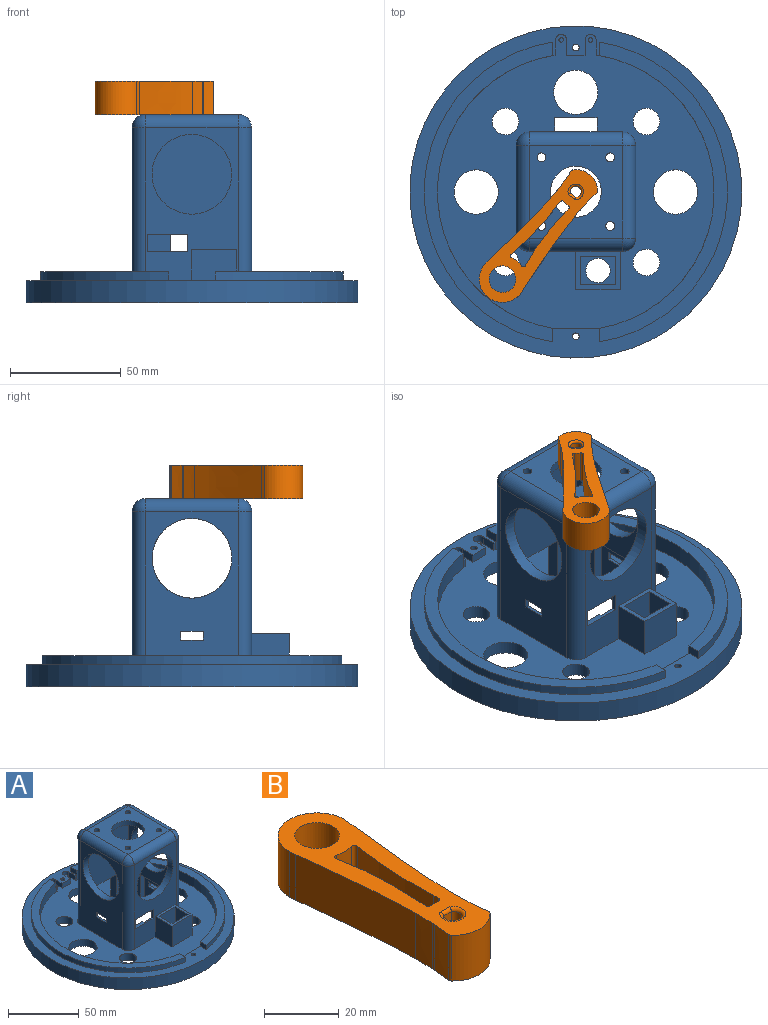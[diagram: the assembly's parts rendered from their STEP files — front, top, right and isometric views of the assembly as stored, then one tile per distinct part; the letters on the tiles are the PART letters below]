
ASSEMBLY  parts=2 mates=1
PART A: 108 faces, bbox 150x150x85 mm
  f0: plane 31.12x5.44mm, normal (0,0,-1), area 142.5mm2, adj f1,f89,f90,f103,f104,f105
  f1: plane 73x42mm, normal (0,1,0), area 2588mm2, adj f0,f11,f64,f70,f73,f89,f103
  f2: plane 10x1.44mm, normal (0,0,-1), area 14.4mm2, adj f3,f5,f17,f101
  f3: plane 4x1.44mm, normal (0,-1,0), area 5.8mm2, adj f2,f4,f17,f101
  f4: plane 10x1.44mm, normal (0,0,1), area 14.4mm2, adj f3,f5,f17,f101
  f5: plane 4x1.44mm, normal (0,1,0), area 5.8mm2, adj f2,f4,f17,f101
  f6: cylinder r=18mm len=36mm, axis (-1,0,0), area 615.2mm2, adj f17,f105
  f7: plane 8x2.64mm, normal (1,0,0), area 21.2mm2, adj f8,f12,f45,f99
  f8: plane 18x2.64mm, normal (0,0,1), area 38.5mm2, adj f7,f9,f12,f97,f98,f99
  f9: plane 8x1.44mm, normal (-1,0,0), area 11.5mm2, adj f8,f12,f45,f97
  f10: cylinder r=18mm len=36mm, axis (0,-1,0), area 615.2mm2, adj f12,f95
  f11: plane 132.88x125mm, normal (0,0,1), area 7587.8mm2, adj f1,f12,f14,f15,f17,f18,f20,f21
  f12: plane 73x42mm, normal (0,-1,0), area 1544.1mm2, adj f7,f8,f9,f10,f11,f45,f62,f66
  f13: plane 16x13mm, normal (0,0,1), area 113mm2, adj f36,f78,f79,f80,f81
  f14: plane 8.29x4mm, normal (0,-1,0), area 33.2mm2, adj f11,f16,f56,f61
  f15: plane 4x0.88mm, normal (0,-1,0), area 3.5mm2, adj f11,f16,f29,f58
  f16: plane 150x150mm, normal (0,0,1), area 3101.6mm2, adj f14,f15,f20,f21,f22,f23,f24,f26
  f17: plane 73x42mm, normal (-1,0,0), area 2008.1mm2, adj f2,f3,f4,f5,f6,f11,f67,f71
  f18: plane 73x42mm, normal (1,0,0), area 2008.1mm2, adj f11,f51,f52,f53,f54,f55,f62,f64
  f19: plane 43.12x43.12mm, normal (0,0,-1), area 1393.6mm2, adj f46,f47,f48,f49,f50,f90,f94,f95
  f20: plane 20x4mm, normal (0,1,0), area 80mm2, adj f11,f16,f29,f34
  f21: plane 4x0.88mm, normal (0,-1,0), area 3.5mm2, adj f11,f16,f34,f59
  f22: cylinder r=1.5mm len=6mm, axis (0,0,-1), area 56.5mm2, adj f16,f75
  f23: cylinder r=75mm len=150mm, axis (0,0,-1), area 4712.4mm2, adj f16,f25
  f24: cylinder r=1.5mm len=6mm, axis (0,0,-1), area 56.5mm2, adj f16,f74
  f25: plane 150x150mm, normal (0,0,-1), area 13601.3mm2, adj f23,f36,f37,f38,f39,f40,f41,f42
  f26: plane 6.08x4mm, normal (1,0,0), area 24.3mm2, adj f16,f28,f29,f30
  f27: plane 6.08x4mm, normal (1,0,0), area 24.3mm2, adj f16,f28,f29,f30
  f28: cylinder r=68.5mm len=135.38mm, axis (0,0,-1), area 776.5mm2, adj f16,f26,f27,f30
  f29: cylinder r=62.5mm len=123.39mm, axis (0,0,-1), area 1406.1mm2, adj f11,f15,f16,f20,f26,f27,f30
  f30: plane 135.38x58mm, normal (0,0,1), area 1108.1mm2, adj f26,f27,f28,f29
  f31: plane 6.08x4mm, normal (-1,0,0), area 24.3mm2, adj f16,f33,f34,f35
  f32: plane 6.08x4mm, normal (-1,0,0), area 24.3mm2, adj f16,f33,f34,f35
  f33: cylinder r=68.5mm len=135.38mm, axis (0,0,-1), area 776.5mm2, adj f16,f31,f32,f35
  f34: cylinder r=62.5mm len=123.39mm, axis (0,0,-1), area 1406.1mm2, adj f11,f16,f20,f21,f31,f32,f35
  f35: plane 135.38x58mm, normal (0,0,1), area 1108.1mm2, adj f31,f32,f33,f34
  f36: cylinder r=5.5mm len=11mm, axis (0,0,-1), area 207.3mm2, adj f13,f25
  f37: cylinder r=6mm len=12mm, axis (0,0,-1), area 226.2mm2, adj f11,f25
  f38: cylinder r=10mm len=20mm, axis (0,0,-1), area 377mm2, adj f11,f25
  f39: cylinder r=6mm len=12mm, axis (0,0,-1), area 226.2mm2, adj f11,f25
  f40: cylinder r=6mm len=12mm, axis (0,0,-1), area 226.2mm2, adj f11,f25
  f41: cylinder r=10mm len=20mm, axis (0,0,-1), area 377mm2, adj f11,f25
  f42: cylinder r=10mm len=20mm, axis (0,0,-1), area 377mm2, adj f11,f25
  f43: cylinder r=6mm len=12mm, axis (0,0,-1), area 226.2mm2, adj f11,f25
  f44: plane 42x42mm, normal (0,0,1), area 1298.3mm2, adj f46,f47,f48,f49,f50,f65,f66,f70
  f45: plane 31.12x5.44mm, normal (0,0,-1), area 148.5mm2, adj f7,f9,f12,f95,f96,f97,f99,f105
  f46: cylinder r=11.5mm len=23mm, axis (0,0,1), area 289mm2, adj f19,f44
  f47: cylinder r=2mm len=4mm, axis (0,0,1), area 50.3mm2, adj f19,f44
  f48: cylinder r=2mm len=4mm, axis (0,0,1), area 50.3mm2, adj f19,f44
  f49: cylinder r=2mm len=4mm, axis (0,0,1), area 50.3mm2, adj f19,f44
  f50: cylinder r=2mm len=4mm, axis (0,0,1), area 50.3mm2, adj f19,f44
  f51: plane 4x1.44mm, normal (0,1,0), area 5.8mm2, adj f18,f52,f54,f92
  f52: plane 10x1.44mm, normal (0,0,1), area 14.4mm2, adj f18,f51,f53,f92
  f53: plane 4x1.44mm, normal (0,-1,0), area 5.8mm2, adj f18,f52,f54,f92
  f54: plane 10x1.44mm, normal (0,0,-1), area 14.4mm2, adj f18,f51,f53,f92
  f55: cylinder r=18mm len=36mm, axis (-1,0,0), area 615.2mm2, adj f18,f94
  f56: plane 6.79x4mm, normal (-1,0,0), area 27.2mm2, adj f11,f14,f16,f57
  f57: cylinder r=2.5mm len=5mm, axis (0,0,-1), area 33.3mm2, adj f11,f16,f56,f58
  f58: plane 6.7x4mm, normal (1,0,0), area 26.8mm2, adj f11,f15,f16,f57
  f59: plane 6.7x4mm, normal (-1,0,0), area 26.8mm2, adj f11,f16,f21,f60
  f60: cylinder r=2.5mm len=5mm, axis (0,0,-1), area 33.3mm2, adj f11,f16,f59,f61
  f61: plane 6.79x4mm, normal (1,0,0), area 27.2mm2, adj f11,f14,f16,f60
  f62: cylinder r=6mm len=73mm, axis (0,0,1), area 688mm2, adj f11,f12,f18,f63
  f63: sphere r=6mm, area 56.5mm2, adj f62,f65,f66
  f64: cylinder r=6mm len=73mm, axis (0,0,-1), area 688mm2, adj f1,f11,f18,f68
  f65: cylinder r=6mm len=42mm, axis (0,-1,0), area 395.8mm2, adj f18,f44,f63,f68
  f66: cylinder r=6mm len=42mm, axis (-1,0,0), area 395.8mm2, adj f12,f44,f63,f69
  f67: cylinder r=6mm len=73mm, axis (0,0,-1), area 688mm2, adj f11,f12,f17,f69
  f68: sphere r=6mm, area 56.5mm2, adj f64,f65,f70
  f69: sphere r=6mm, area 56.5mm2, adj f66,f67,f71
  f70: cylinder r=6mm len=42mm, axis (1,0,0), area 395.8mm2, adj f1,f44,f68,f72
  f71: cylinder r=6mm len=42mm, axis (0,1,0), area 395.8mm2, adj f17,f44,f69,f72
  f72: sphere r=6mm, area 56.5mm2, adj f70,f71,f73
  f73: cylinder r=6mm len=73mm, axis (0,0,1), area 688mm2, adj f1,f11,f17,f72
  f74: cone r=5.5mm half-angle=45deg, axis (0,0,-1), area 124.4mm2, adj f24,f25
  f75: cone r=5.5mm half-angle=45deg, axis (0,0,-1), area 124.4mm2, adj f22,f25
  f76: plane 20x18mm, normal (0,-1,0), area 360mm2, adj f11,f77,f82,f83
  f77: plane 18x17mm, normal (1,0,0), area 306mm2, adj f11,f12,f76,f83
  f78: plane 18x13mm, normal (1,0,0), area 234mm2, adj f13,f79,f81,f83
  f79: plane 18x16mm, normal (0,-1,0), area 288mm2, adj f13,f78,f80,f83
  f80: plane 18x13mm, normal (-1,0,0), area 234mm2, adj f13,f79,f81,f83
  f81: plane 18x16mm, normal (0,1,0), area 288mm2, adj f13,f78,f80,f83
  f82: plane 18x17mm, normal (-1,0,0), area 306mm2, adj f11,f12,f76,f83
  f83: plane 20x17mm, normal (0,0,1), area 132mm2, adj f12,f76,f77,f78,f79,f80,f81,f82
  f84: cylinder r=1mm len=2mm, axis (0,0,-1), area 12.6mm2, adj f11,f85
  f85: plane 2x2mm, normal (0,0,1), area 3.1mm2, adj f84
  f86: cylinder r=1mm len=2mm, axis (0,0,-1), area 12.6mm2, adj f11,f87
  f87: plane 2x2mm, normal (0,0,1), area 3.1mm2, adj f86
  f88: plane 19.12x6mm, normal (0,-1,0), area 114.7mm2, adj f11,f25,f89,f103
  f89: plane 31x12mm, normal (-1,0,0), area 208mm2, adj f0,f1,f11,f25,f88,f90
  f90: plane 81x43.12mm, normal (0,-1,0), area 2528mm2, adj f0,f19,f25,f89,f94,f105
  f91: plane 31x4mm, normal (0,-1,0), area 124mm2, adj f25,f92,f94,f106
  f92: plane 31x19.12mm, normal (-1,0,0), area 552.7mm2, adj f25,f51,f52,f53,f54,f91,f93,f106
  f93: plane 31x4mm, normal (0,1,0), area 124mm2, adj f25,f92,f94,f106
  f94: plane 81x43.12mm, normal (-1,0,0), area 1882.1mm2, adj f19,f25,f55,f90,f91,f93,f95,f106
  f95: plane 81x43.12mm, normal (0,1,0), area 1510.1mm2, adj f10,f19,f25,f45,f94,f96,f105
  f96: plane 31x4mm, normal (-1,0,0), area 124mm2, adj f25,f45,f95,f97
  f97: plane 31x19.12mm, normal (0,1,0), area 532.2mm2, adj f8,f9,f25,f45,f96,f98
  f98: plane 23x1.2mm, normal (1,0,0), area 27.7mm2, adj f8,f25,f97,f99
  f99: plane 31x12mm, normal (0,1,0), area 288.5mm2, adj f7,f8,f25,f45,f98,f105
  f100: plane 31x4mm, normal (0,1,0), area 124mm2, adj f25,f101,f105,f107
  f101: plane 31x19.12mm, normal (1,0,0), area 552.7mm2, adj f2,f3,f4,f5,f25,f100,f102,f107
  f102: plane 31x4mm, normal (0,-1,0), area 124mm2, adj f25,f101,f105,f107
  f103: plane 31x8.8mm, normal (1,0,0), area 108.7mm2, adj f0,f1,f11,f25,f88,f104
  f104: plane 31x12mm, normal (0,-1,0), area 372mm2, adj f0,f25,f103,f105
  f105: plane 81x49.12mm, normal (1,0,0), area 2068.1mm2, adj f0,f6,f19,f25,f45,f90,f95,f99
  f106: plane 19.12x4mm, normal (0,0,-1), area 76.5mm2, adj f91,f92,f93,f94
  f107: plane 19.12x4mm, normal (0,0,-1), area 76.5mm2, adj f100,f101,f102,f105
PART B: 33 faces, bbox 21x72x15 mm
  f0: extruded ~15x2.23mm, area 33.7mm2, adj f1,f17,f21,f22
  f1: cylinder r=10.5mm len=21mm, axis (0,0,-1), area 494.8mm2, adj f0,f2,f21,f22
  f2: extruded ~15x2.23mm, area 33.7mm2, adj f1,f3,f21,f22
  f3: extruded ~41.94x15mm, area 631.5mm2, adj f2,f4,f21,f22
  f4: extruded ~15x6.5mm, area 97.6mm2, adj f3,f5,f21,f22
  f5: extruded ~15x0.82mm, area 12.3mm2, adj f4,f6,f21,f22
  f6: extruded ~15x5.98mm, area 90.1mm2, adj f5,f21,f22,f27
  f7: cylinder r=10mm len=15mm, axis (0,0,-1), area 247.3mm2, adj f21,f22,f27,f28
  f8: extruded ~15x5.98mm, area 90.1mm2, adj f9,f21,f22,f28
  f9: extruded ~15x0.82mm, area 12.3mm2, adj f8,f10,f21,f22
  f10: extruded ~15x6.5mm, area 97.6mm2, adj f9,f17,f21,f22
  f11: cylinder r=2.5mm len=13mm, axis (0,0,-1), area 162.4mm2, adj f18,f29,f32
  f12: extruded ~30.47x15mm, area 459.2mm2, adj f19,f21,f22,f23
  f13: cylinder r=10.5mm len=15mm, axis (0,0,-1), area 85.9mm2, adj f21,f22,f23,f24
  f14: extruded ~30.55x15mm, area 460mm2, adj f15,f21,f22,f24
  f15: extruded ~15x1.79mm, area 26.9mm2, adj f14,f21,f22,f26
  f16: cylinder r=7mm len=15mm, axis (0,0,-1), area 39.6mm2, adj f21,f22,f25,f26
  f17: extruded ~41.94x15mm, area 631.5mm2, adj f0,f10,f21,f22
  f18: plane 13x3mm, normal (0,-1,0), area 39mm2, adj f11,f30,f31
  f19: extruded ~15x1.78mm, area 26.8mm2, adj f12,f21,f22,f25
  f20: cylinder r=6mm len=15mm, axis (0,0,-1), area 565.5mm2, adj f21,f22
  f21: plane 72x21mm, normal (0,0,1), area 810.8mm2, adj f0,f1,f2,f3,f4,f5,f6,f7
  f22: plane 72x21mm, normal (0,0,-1), area 810.8mm2, adj f0,f1,f2,f3,f4,f5,f6,f7
  f23: cylinder r=1mm len=15mm, axis (0,0,-1), area 31mm2, adj f12,f13,f21,f22
  f24: cylinder r=1mm len=15mm, axis (0,0,-1), area 30.4mm2, adj f13,f14,f21,f22
  f25: cylinder r=1mm len=15mm, axis (0,0,-1), area 27.5mm2, adj f16,f19,f21,f22
  f26: cylinder r=1mm len=15mm, axis (0,0,-1), area 27.3mm2, adj f15,f16,f21,f22
  f27: cylinder r=1mm len=15mm, axis (0,0,-1), area 13.2mm2, adj f6,f7,f21,f22
  f28: cylinder r=1mm len=15mm, axis (0,0,-1), area 13.2mm2, adj f7,f8,f21,f22
  f29: torus R=3.5mm, axis (0,0,1), area 22.9mm2, adj f11,f22,f30
  f30: cylinder r=1mm len=3.61mm, axis (1,0,0), area 5.1mm2, adj f18,f22,f29
  f31: cylinder r=1mm len=3.61mm, axis (-1,0,0), area 5.1mm2, adj f18,f21,f32
  f32: torus R=3.5mm, axis (0,0,1), area 22.9mm2, adj f11,f21,f31
PLACE A t=(27.68,101.23,0)mm
PLACE B rot(axis=(0,0,1),140deg) t=(-48.97,165.45,85)mm
MATE revolute B.f22 <-> A.f46  axis (0,0,-1) through (27.68,101.23,85)mm
